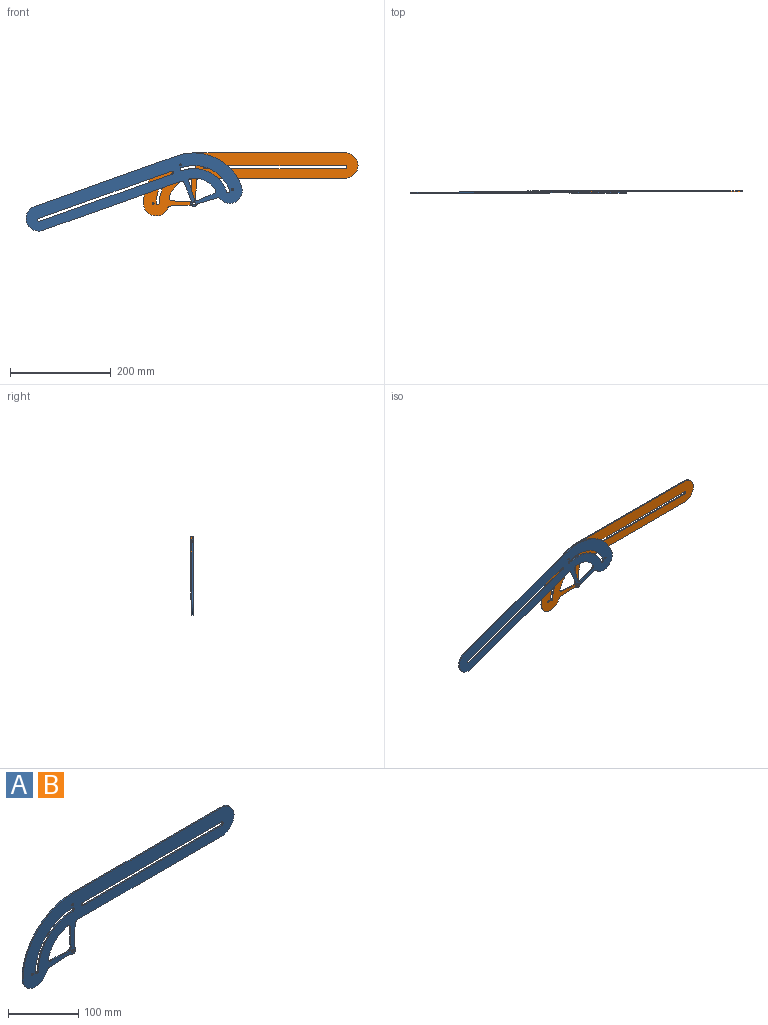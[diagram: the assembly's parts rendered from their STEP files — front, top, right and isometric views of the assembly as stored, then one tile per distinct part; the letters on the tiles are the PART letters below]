
ASSEMBLY  parts=2 mates=1
PART A: 35 faces, bbox 425x2x125 mm
  f0: cylinder r=3mm len=6mm, axis (0,1,0), area 18.8mm2, adj f1,f15,f20,f21
  f1: plane 279x2mm, normal (0,0,1), area 558mm2, adj f0,f2,f20,f21
  f2: cylinder r=3mm len=6mm, axis (0,1,0), area 18.8mm2, adj f1,f15,f20,f21
  f3: plane 35.71x2mm, normal (0.05,0,1), area 71.5mm2, adj f20,f21,f23,f28
  f4: cylinder r=50mm len=37.59mm, axis (0,1,0), area 112.1mm2, adj f20,f21,f23,f25
  f5: cylinder r=25mm len=48.51mm, axis (0,1,0), area 139.8mm2, adj f17,f20,f21,f22
  f6: plane 39.37x2.06mm, normal (0.05,0,-1), area 78.8mm2, adj f20,f21,f22,f24
  f7: cylinder r=6mm len=10.05mm, axis (0,1,0), area 36.6mm2, adj f20,f21,f24,f27
  f8: plane 37.58x2mm, normal (1,0,-0.05), area 75.3mm2, adj f20,f21,f26,f27
  f9: plane 289.91x2mm, normal (0,0,-1), area 579.8mm2, adj f10,f20,f21,f26
  f10: cylinder r=25mm len=50mm, axis (0,1,0), area 157.1mm2, adj f9,f11,f20,f21
  f11: plane 300x2mm, normal (0,0,1), area 600mm2, adj f10,f17,f20,f21
  f12: cylinder r=3mm len=6mm, axis (0,1,0), area 18.8mm2, adj f13,f18,f20,f21
  f13: cylinder r=69mm len=69mm, axis (0,1,0), area 216.8mm2, adj f12,f14,f20,f21
  f14: cylinder r=3mm len=6mm, axis (0,1,0), area 18.8mm2, adj f13,f18,f20,f21
  f15: plane 279x2mm, normal (0,0,-1), area 558mm2, adj f0,f2,f20,f21
  f16: plane 35.71x2mm, normal (-1,0,-0.05), area 71.5mm2, adj f20,f21,f25,f28
  f17: cylinder r=100mm len=100mm, axis (0,1,0), area 314.2mm2, adj f5,f11,f20,f21
  f18: cylinder r=75mm len=75mm, axis (0,1,0), area 235.6mm2, adj f12,f14,f20,f21
  f19: cylinder r=3mm len=6mm, axis (0,1,0), area 37.7mm2, adj f20,f21
  f20: plane 425x125mm, normal (0,-1,0), area 21274mm2, adj f0,f1,f2,f3,f4,f5,f6,f7
  f21: plane 425x125mm, normal (0,1,0), area 21274mm2, adj f0,f1,f2,f3,f4,f5,f6,f7
  f22: cylinder r=5mm len=4.44mm, axis (0,1,0), area 11.7mm2, adj f5,f6,f20,f21
  f23: cylinder r=5mm len=6.11mm, axis (0,1,0), area 17.4mm2, adj f3,f4,f20,f21
  f24: cylinder r=5mm len=3.63mm, axis (0,1,0), area 7.9mm2, adj f6,f7,f20,f21
  f25: cylinder r=5mm len=6.11mm, axis (0,1,0), area 17.4mm2, adj f4,f16,f20,f21
  f26: cylinder r=5mm len=4.99mm, axis (0,-1,0), area 15.2mm2, adj f8,f9,f20,f21
  f27: cylinder r=5mm len=3.63mm, axis (0,1,0), area 7.9mm2, adj f7,f8,f20,f21
  f28: cylinder r=5mm len=5.26mm, axis (0,1,0), area 16.8mm2, adj f3,f16,f20,f21
  f29: cylinder r=2mm len=4mm, axis (0,-1,0), area 22.6mm2, adj f20,f21,f30,f31
  f30: plane 2x0.9mm, normal (0.82,0,-0.57), area 2.2mm2, adj f20,f21,f29,f31
  f31: plane 2x0.9mm, normal (-0.82,0,-0.57), area 2.2mm2, adj f20,f21,f29,f30
  f32: cylinder r=2mm len=4mm, axis (0,-1,0), area 22.6mm2, adj f20,f21,f33,f34
  f33: plane 2x0.9mm, normal (0.57,0,0.82), area 2.2mm2, adj f20,f21,f32,f34
  f34: plane 2x0.9mm, normal (0.57,0,-0.82), area 2.2mm2, adj f20,f21,f32,f33
PART B: same geometry as A
PLACE A rot(axis=(0.17,0,-0.99),180deg) t=(-17.02,-5.28,9.82)mm
PLACE B t=(-17.02,-3.28,9.82)mm fixed
MATE revolute A.f4 <-> B.f4  axis (0,-1,0) through (-17.02,-4.28,9.82)mm
